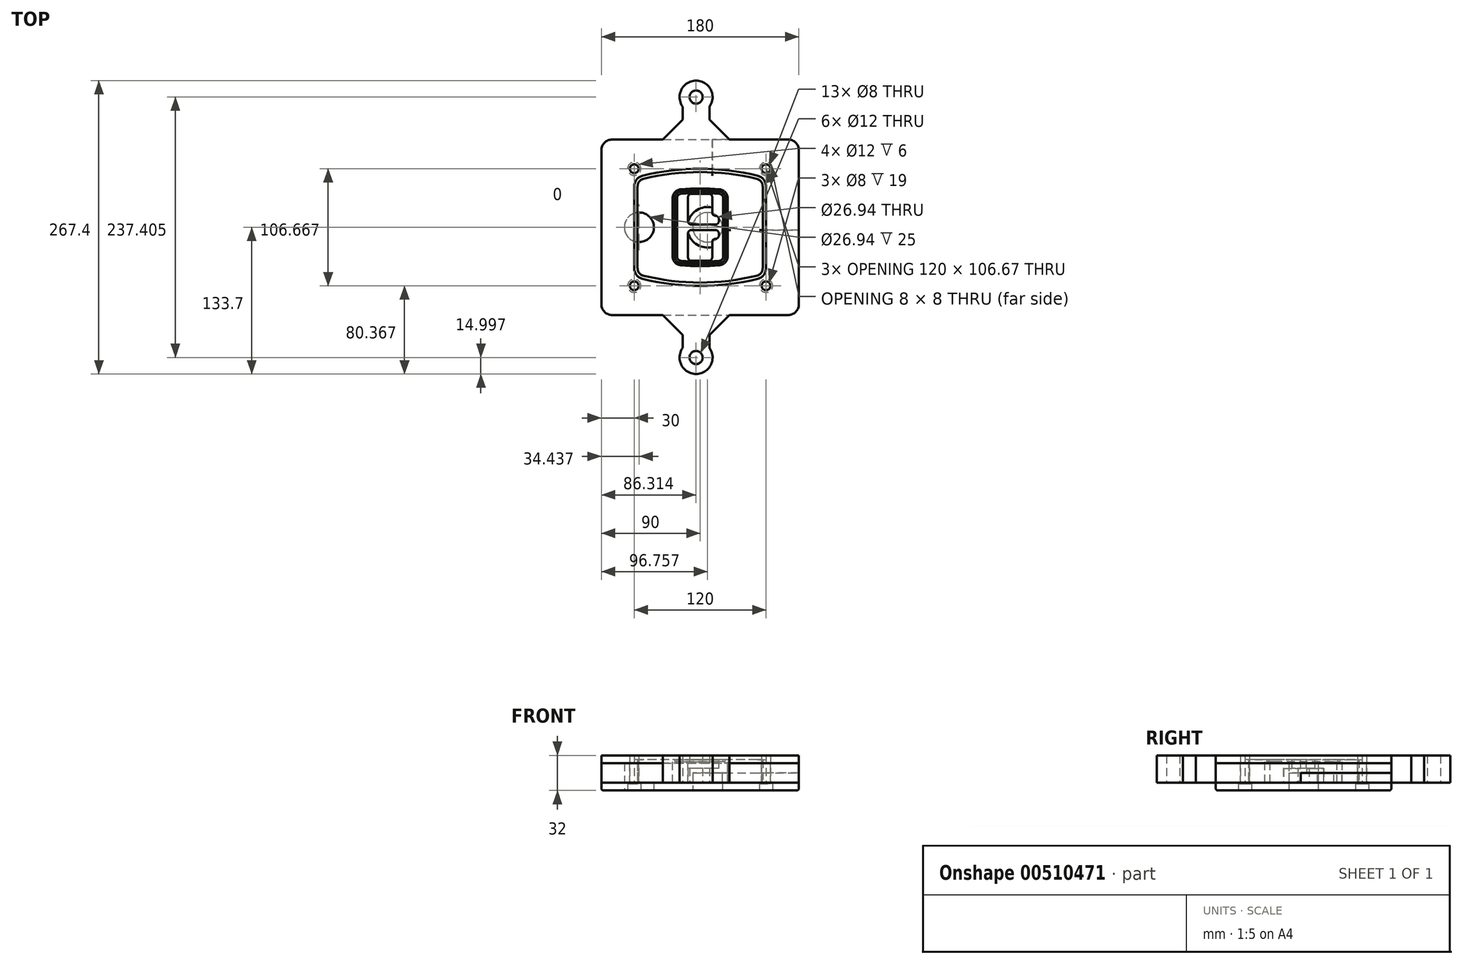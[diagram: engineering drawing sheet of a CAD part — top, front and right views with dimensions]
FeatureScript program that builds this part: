
annotation { "Feature Type Name" : "Feature", "Feature Type Description" : "" }
export const myFeature = defineFeature(function(context is Context, id is Id, definition is map)
    precondition{}
    {
        {
            var Q0;
            Q0=qCreatedBy(makeId("Top.planeOp"),FACE);
            var sketch = newSketch(context, id + "F0", { "sketchPlane" : qUnion([Q0])});
            skPoint(sketch, "E0.rect.middle", {"position": v(0, 0) * mm});
            skLineSegment(sketch, "E1.bottom", {"start": v(-80, -80) * mm, "end": v(80, -80) * mm});
            skLineSegment(sketch, "E1.top", {"start": v(-80, 80) * mm, "end": v(80, 80) * mm});
            skLineSegment(sketch, "E1.left", {"start": v(-90, -70) * mm, "end": v(-90, 70) * mm});
            skLineSegment(sketch, "E1.right", {"start": v(90, -70) * mm, "end": v(90, 70) * mm});
            skLineSegment(sketch, "E2", {"start": v(-90, 80) * mm, "end": v(90, -80) * mm, "construction": true});
            skLineSegment(sketch, "E3", {"start": v(90, 80) * mm, "end": v(-90, -80) * mm, "construction": true});
            skCircle(sketch, "E4", {"center": v(-60, 53.33) * mm, "radius": 4 * mm});
            skCircle(sketch, "E5", {"center": v(60, 53.33) * mm, "radius": 4 * mm});
            skCircle(sketch, "E6", {"center": v(60, -53.33) * mm, "radius": 4 * mm});
            skCircle(sketch, "E7", {"center": v(-60, -53.33) * mm, "radius": 4 * mm});
            skLineSegment(sketch, "E8", {"start": v(-60, 53.33) * mm, "end": v(60, 53.33) * mm, "construction": true});
            skLineSegment(sketch, "E9", {"start": v(60, 53.33) * mm, "end": v(60, -53.33) * mm, "construction": true});
            skLineSegment(sketch, "E10", {"start": v(60, -53.33) * mm, "end": v(-60, -53.33) * mm, "construction": true});
            skLineSegment(sketch, "E11", {"start": v(-60, -53.33) * mm, "end": v(-60, 53.33) * mm, "construction": true});
            skLineSegment(sketch, "E12", {"start": v(-60, 37.3) * mm, "end": v(-60, -37.3) * mm});
            skLineSegment(sketch, "E13", {"start": v(60, 37.3) * mm, "end": v(60, -37.3) * mm});
            skArc(sketch, "E14", {"start": v(52.38, 47.01) * mm, "mid": v(0, 53.33) * mm, "end": v(-52.38, 47.01) * mm});
            skArc(sketch, "E15", {"start": v(-52.38, -47.01) * mm, "mid": v(0, -53.33) * mm, "end": v(52.38, -47.01) * mm});
            skLineSegment(sketch, "E16", {"start": v(-60, 0) * mm, "end": v(60, 0) * mm, "construction": true});
            skPoint(sketch, "E17.visualSharp", {"position": v(-60, -45) * mm});
            skArc(sketch, "E17.filletArc", {"start": v(-60, -37.3) * mm, "mid": v(-57.87, -43.47) * mm, "end": v(-52.38, -47.01) * mm});
            skPoint(sketch, "E18.visualSharp", {"position": v(-60, 45) * mm});
            skArc(sketch, "E18.filletArc", {"start": v(-52.38, 47.01) * mm, "mid": v(-57.87, 43.47) * mm, "end": v(-60, 37.3) * mm});
            skPoint(sketch, "E19.visualSharp", {"position": v(60, 45) * mm});
            skArc(sketch, "E19.filletArc", {"start": v(60, 37.3) * mm, "mid": v(57.87, 43.47) * mm, "end": v(52.38, 47.01) * mm});
            skPoint(sketch, "E20.visualSharp", {"position": v(60, -45) * mm});
            skArc(sketch, "E20.filletArc", {"start": v(52.38, -47.01) * mm, "mid": v(57.87, -43.47) * mm, "end": v(60, -37.3) * mm});
            skPoint(sketch, "E21.visualSharp", {"position": v(-90, 80) * mm});
            skArc(sketch, "E21.filletArc", {"start": v(-80, 80) * mm, "mid": v(-87.07, 77.07) * mm, "end": v(-90, 70) * mm});
            skPoint(sketch, "E22.visualSharp", {"position": v(90, 80) * mm});
            skArc(sketch, "E22.filletArc", {"start": v(90, 70) * mm, "mid": v(87.07, 77.07) * mm, "end": v(80, 80) * mm});
            skPoint(sketch, "E23.visualSharp", {"position": v(90, -80) * mm});
            skArc(sketch, "E23.filletArc", {"start": v(80, -80) * mm, "mid": v(87.07, -77.07) * mm, "end": v(90, -70) * mm});
            skPoint(sketch, "E24.visualSharp", {"position": v(-90, -80) * mm});
            skArc(sketch, "E24.filletArc", {"start": v(-90, -70) * mm, "mid": v(-87.07, -77.07) * mm, "end": v(-80, -80) * mm});
            skArc(sketch, "E25.0", {"start": v(57, 37.3) * mm, "mid": v(55.5, 41.62) * mm, "end": v(51.67, 44.1) * mm});
            skLineSegment(sketch, "E25.1", {"start": v(57, 37.3) * mm, "end": v(57, -37.3) * mm});
            skArc(sketch, "E25.2", {"start": v(51.67, -44.1) * mm, "mid": v(55.5, -41.62) * mm, "end": v(57, -37.3) * mm});
            skArc(sketch, "E25.3", {"start": v(-51.67, -44.1) * mm, "mid": v(0, -50.33) * mm, "end": v(51.67, -44.1) * mm});
            skArc(sketch, "E25.4", {"start": v(-57, -37.3) * mm, "mid": v(-55.5, -41.62) * mm, "end": v(-51.67, -44.1) * mm});
            skArc(sketch, "E25.5", {"start": v(51.67, 44.1) * mm, "mid": v(0, 50.33) * mm, "end": v(-51.67, 44.1) * mm});
            skLineSegment(sketch, "E25.6", {"start": v(-57, 37.3) * mm, "end": v(-57, -37.3) * mm});
            skArc(sketch, "E25.7", {"start": v(-51.67, 44.1) * mm, "mid": v(-55.5, 41.62) * mm, "end": v(-57, 37.3) * mm});
            skArc(sketch, "E26.0", {"start": v(-53.33, 50.9) * mm, "mid": v(-61.01, 45.94) * mm, "end": v(-64, 37.3) * mm});
            skArc(sketch, "E26.1", {"start": v(53.33, 50.9) * mm, "mid": v(0, 57.33) * mm, "end": v(-53.33, 50.9) * mm});
            skArc(sketch, "E26.2", {"start": v(64, 37.3) * mm, "mid": v(61.01, 45.94) * mm, "end": v(53.33, 50.9) * mm});
            skLineSegment(sketch, "E26.3", {"start": v(64, 37.3) * mm, "end": v(64, -37.3) * mm});
            skArc(sketch, "E26.4", {"start": v(53.33, -50.9) * mm, "mid": v(61.01, -45.94) * mm, "end": v(64, -37.3) * mm});
            skLineSegment(sketch, "E26.5", {"start": v(-64, 37.3) * mm, "end": v(-64, -37.3) * mm});
            skArc(sketch, "E26.6", {"start": v(-53.33, -50.9) * mm, "mid": v(0, -57.33) * mm, "end": v(53.33, -50.9) * mm});
            skArc(sketch, "E26.7", {"start": v(-64, -37.3) * mm, "mid": v(-61.01, -45.94) * mm, "end": v(-53.33, -50.9) * mm});
            skSolve(sketch);
        }
        {
            var Q0;
            Q0=makeQuery(id+"F0.imprint","IMPRINT",FACE,{"disambiguationData":[TD([[makeQuery(id+"F0.imprint","IMPRINT",EDGE,{"derivedFrom":sQuery(id+"F0.wireOp",EDGE,"E1.bottom")}),1.0]])]});
            var Q1;
            Q1=makeQuery(id+"F0.imprint","IMPRINT",FACE,{"disambiguationData":[TD([[makeQuery(id+"F0.imprint","IMPRINT",EDGE,{"derivedFrom":sQuery(id+"F0.wireOp",EDGE,"E12")}),1.0]])]});
            var Q2;
            Q2=makeQuery(id+"F0.imprint","IMPRINT",FACE,{"disambiguationData":[TD([[makeQuery(id+"F0.imprint","IMPRINT",EDGE,{"derivedFrom":sQuery(id+"F0.wireOp",EDGE,"E25.0")}),1.0]])]});
            var Q3;
            Q3=makeQuery(id+"F0.imprint","IMPRINT",FACE,{"disambiguationData":[TD([[makeQuery(id+"F0.imprint","IMPRINT",EDGE,{"derivedFrom":sQuery(id+"F0.wireOp",EDGE,"E12")}),-1.0]])]});
            extrude(context, id + "F1", {"entities" : qUnion([Q0, Q1, Q2, Q3]), "oppositeDirection" : true, "depth" : 25 * mm});
        }
        {
            var Q0;
            Q0=makeQuery(id+"F0.imprint","IMPRINT",FACE,{"disambiguationData":[TD([[makeQuery(id+"F0.imprint","IMPRINT",EDGE,{"derivedFrom":sQuery(id+"F0.wireOp",EDGE,"E12")}),1.0]])]});
            extrude(context, id + "F2", {"entities" : qUnion([Q0]), "operationType" : NewBodyOperationType.ADD, "depth" : 3 * mm});
        }
        {
            var Q0;
            Q0=makeQuery(id+"F0.imprint","IMPRINT",FACE,{"disambiguationData":[TD([[makeQuery(id+"F0.imprint","IMPRINT",EDGE,{"derivedFrom":sQuery(id+"F0.wireOp",EDGE,"E25.0")}),1.0]])]});
            extrude(context, id + "F3", {"entities" : qUnion([Q0]), "operationType" : NewBodyOperationType.REMOVE, "oppositeDirection" : true, "depth" : 18 * mm});
        }
        {
            var Q0;
            Q0=makeQuery(id+"F2.opExtrude","CAP_FACE",FACE,{"disambiguationData":[OSD([sQuery(id+"F0.wireOp",EDGE,"E12"),sQuery(id+"F0.wireOp",EDGE,"E13"),sQuery(id+"F0.wireOp",EDGE,"E14"),sQuery(id+"F0.wireOp",EDGE,"E15"),sQuery(id+"F0.wireOp",EDGE,"E17.filletArc"),sQuery(id+"F0.wireOp",EDGE,"E18.filletArc"),sQuery(id+"F0.wireOp",EDGE,"E19.filletArc"),sQuery(id+"F0.wireOp",EDGE,"E20.filletArc"),sQuery(id+"F0.wireOp",EDGE,"E25.0"),sQuery(id+"F0.wireOp",EDGE,"E25.1"),sQuery(id+"F0.wireOp",EDGE,"E25.2"),sQuery(id+"F0.wireOp",EDGE,"E25.3"),sQuery(id+"F0.wireOp",EDGE,"E25.4"),sQuery(id+"F0.wireOp",EDGE,"E25.5"),sQuery(id+"F0.wireOp",EDGE,"E25.6"),sQuery(id+"F0.wireOp",EDGE,"E25.7")])],"isStart":false});
            var sketch = newSketch(context, id + "F4", { "sketchPlane" : qUnion([Q0])});
            skArc(sketch, "E27.0", {"start": v(-17.7, -34.56) * mm, "mid": v(0, -35.33) * mm, "end": v(17.7, -34.56) * mm});
            skArc(sketch, "E28.0", {"start": v(17.7, 34.56) * mm, "mid": v(0, 35.33) * mm, "end": v(-17.7, 34.56) * mm});
            skLineSegment(sketch, "E29", {"start": v(-25, 26.59) * mm, "end": v(-25, -26.59) * mm});
            skLineSegment(sketch, "E30", {"start": v(25, 26.59) * mm, "end": v(25, -26.59) * mm});
            skLineSegment(sketch, "E31", {"start": v(-25, 33.78) * mm, "end": v(25, 33.78) * mm, "construction": true});
            skLineSegment(sketch, "E32", {"start": v(-25, -33.78) * mm, "end": v(25, -33.78) * mm, "construction": true});
            skPoint(sketch, "E33.visualSharp", {"position": v(-25, 33.78) * mm});
            skArc(sketch, "E33.filletArc", {"start": v(-17.7, 34.56) * mm, "mid": v(-22.9, 32) * mm, "end": v(-25, 26.59) * mm});
            skPoint(sketch, "E34.visualSharp", {"position": v(25, 33.78) * mm});
            skArc(sketch, "E34.filletArc", {"start": v(25, 26.59) * mm, "mid": v(22.9, 32) * mm, "end": v(17.7, 34.56) * mm});
            skPoint(sketch, "E35.visualSharp", {"position": v(25, -33.78) * mm});
            skArc(sketch, "E35.filletArc", {"start": v(17.7, -34.56) * mm, "mid": v(22.9, -32) * mm, "end": v(25, -26.59) * mm});
            skPoint(sketch, "E36.visualSharp", {"position": v(-25, -33.78) * mm});
            skArc(sketch, "E36.filletArc", {"start": v(-25, -26.59) * mm, "mid": v(-22.9, -32) * mm, "end": v(-17.7, -34.56) * mm});
            skArc(sketch, "E37.0", {"start": v(51.67, 44.1) * mm, "mid": v(0, 50.33) * mm, "end": v(-51.67, 44.1) * mm});
            skArc(sketch, "E37.1", {"start": v(-51.67, 44.1) * mm, "mid": v(-55.5, 41.62) * mm, "end": v(-57, 37.3) * mm});
            skLineSegment(sketch, "E37.2", {"start": v(-57, 37.3) * mm, "end": v(-57, -37.3) * mm});
            skArc(sketch, "E37.3", {"start": v(-57, -37.3) * mm, "mid": v(-55.5, -41.62) * mm, "end": v(-51.67, -44.1) * mm});
            skArc(sketch, "E37.4", {"start": v(-51.67, -44.1) * mm, "mid": v(0, -50.33) * mm, "end": v(51.67, -44.1) * mm});
            skArc(sketch, "E37.5", {"start": v(51.67, -44.1) * mm, "mid": v(55.5, -41.62) * mm, "end": v(57, -37.3) * mm});
            skLineSegment(sketch, "E37.6", {"start": v(57, 37.3) * mm, "end": v(57, -37.3) * mm});
            skArc(sketch, "E37.7", {"start": v(57, 37.3) * mm, "mid": v(55.5, 41.62) * mm, "end": v(51.67, 44.1) * mm});
            skLineSegment(sketch, "E38.0", {"start": v(23, 26.59) * mm, "end": v(23, -26.59) * mm});
            skArc(sketch, "E38.1", {"start": v(17.53, -32.56) * mm, "mid": v(21.42, -30.64) * mm, "end": v(23, -26.59) * mm});
            skArc(sketch, "E38.2", {"start": v(-17.53, -32.56) * mm, "mid": v(0, -33.33) * mm, "end": v(17.53, -32.56) * mm});
            skArc(sketch, "E38.3", {"start": v(-23, -26.59) * mm, "mid": v(-21.42, -30.64) * mm, "end": v(-17.53, -32.56) * mm});
            skLineSegment(sketch, "E38.4", {"start": v(-23, 26.59) * mm, "end": v(-23, -26.59) * mm});
            skArc(sketch, "E38.5", {"start": v(23, 26.59) * mm, "mid": v(21.42, 30.64) * mm, "end": v(17.53, 32.56) * mm});
            skArc(sketch, "E38.6", {"start": v(-17.53, 32.56) * mm, "mid": v(-21.42, 30.64) * mm, "end": v(-23, 26.59) * mm});
            skArc(sketch, "E38.7", {"start": v(17.53, 32.56) * mm, "mid": v(0, 33.33) * mm, "end": v(-17.53, 32.56) * mm});
            skArc(sketch, "E39.0", {"start": v(21, 26.59) * mm, "mid": v(19.95, 29.29) * mm, "end": v(17.35, 30.57) * mm});
            skLineSegment(sketch, "E39.1", {"start": v(21, 26.59) * mm, "end": v(21, -26.59) * mm});
            skArc(sketch, "E39.2", {"start": v(17.35, -30.57) * mm, "mid": v(19.95, -29.29) * mm, "end": v(21, -26.59) * mm});
            skArc(sketch, "E39.3", {"start": v(-17.35, -30.57) * mm, "mid": v(0, -31.33) * mm, "end": v(17.35, -30.57) * mm});
            skArc(sketch, "E39.4", {"start": v(-21, -26.59) * mm, "mid": v(-19.95, -29.29) * mm, "end": v(-17.35, -30.57) * mm});
            skArc(sketch, "E39.5", {"start": v(17.35, 30.57) * mm, "mid": v(0, 31.33) * mm, "end": v(-17.35, 30.57) * mm});
            skLineSegment(sketch, "E39.6", {"start": v(-21, 26.59) * mm, "end": v(-21, -26.59) * mm});
            skArc(sketch, "E39.7", {"start": v(-17.35, 30.57) * mm, "mid": v(-19.95, 29.29) * mm, "end": v(-21, 26.59) * mm});
            skLineSegment(sketch, "E40", {"start": v(-25, 0) * mm, "end": v(25, 0) * mm, "construction": true});
            skLineSegment(sketch, "E41", {"start": v(-11, 5.5) * mm, "end": v(-11, 27.5) * mm});
            skLineSegment(sketch, "E42", {"start": v(-8, 30.5) * mm, "end": v(8, 30.5) * mm});
            skLineSegment(sketch, "E43", {"start": v(11, 27.5) * mm, "end": v(11, 13.5) * mm});
            skLineSegment(sketch, "E44", {"start": v(14, 10.5) * mm, "end": v(14, 10.5) * mm});
            skLineSegment(sketch, "E45", {"start": v(17, 7.5) * mm, "end": v(17, 5.5) * mm});
            skLineSegment(sketch, "E46", {"start": v(14, 2.5) * mm, "end": v(-8, 2.5) * mm});
            skPoint(sketch, "E47.visualSharp", {"position": v(-11, 30.5) * mm});
            skArc(sketch, "E47.filletArc", {"start": v(-8, 30.5) * mm, "mid": v(-10.12, 29.62) * mm, "end": v(-11, 27.5) * mm});
            skPoint(sketch, "E48.visualSharp", {"position": v(11, 30.5) * mm});
            skArc(sketch, "E48.filletArc", {"start": v(11, 27.5) * mm, "mid": v(10.12, 29.62) * mm, "end": v(8, 30.5) * mm});
            skPoint(sketch, "E49.visualSharp", {"position": v(11, 10.5) * mm});
            skArc(sketch, "E49.filletArc", {"start": v(11, 13.5) * mm, "mid": v(11.88, 11.38) * mm, "end": v(14, 10.5) * mm});
            skPoint(sketch, "E50.visualSharp", {"position": v(17, 10.5) * mm});
            skArc(sketch, "E50.filletArc", {"start": v(17, 7.5) * mm, "mid": v(16.12, 9.62) * mm, "end": v(14, 10.5) * mm});
            skPoint(sketch, "E51.visualSharp", {"position": v(17, 2.5) * mm});
            skArc(sketch, "E51.filletArc", {"start": v(14, 2.5) * mm, "mid": v(16.12, 3.38) * mm, "end": v(17, 5.5) * mm});
            skPoint(sketch, "E52.visualSharp", {"position": v(-11, 2.5) * mm});
            skArc(sketch, "E52.filletArc", {"start": v(-11, 5.5) * mm, "mid": v(-10.12, 3.38) * mm, "end": v(-8, 2.5) * mm});
            skLineSegment(sketch, "E53.0.MirrorCS", {"start": v(14, -2.5) * mm, "end": v(-8, -2.5) * mm});
            skArc(sketch, "E54.0.MirrorCS", {"start": v(-11, -5.5) * mm, "mid": v(-10.12, -3.38) * mm, "end": v(-8, -2.5) * mm});
            skLineSegment(sketch, "E55.0.MirrorCS", {"start": v(-11, -5.5) * mm, "end": v(-11, -27.5) * mm});
            skArc(sketch, "E56.0.MirrorCS", {"start": v(-8, -30.5) * mm, "mid": v(-10.12, -29.62) * mm, "end": v(-11, -27.5) * mm});
            skLineSegment(sketch, "E57.0.MirrorCS", {"start": v(-8, -30.5) * mm, "end": v(8, -30.5) * mm});
            skArc(sketch, "E58.0.MirrorCS", {"start": v(11, -27.5) * mm, "mid": v(10.12, -29.62) * mm, "end": v(8, -30.5) * mm});
            skLineSegment(sketch, "E59.0.MirrorCS", {"start": v(11, -27.5) * mm, "end": v(11, -13.5) * mm});
            skArc(sketch, "E60.0.MirrorCS", {"start": v(11, -13.5) * mm, "mid": v(11.88, -11.38) * mm, "end": v(14, -10.5) * mm});
            skArc(sketch, "E61.0.MirrorCS", {"start": v(17, -7.5) * mm, "mid": v(16.12, -9.62) * mm, "end": v(14, -10.5) * mm});
            skLineSegment(sketch, "E62.0.MirrorCS", {"start": v(17, -7.5) * mm, "end": v(17, -5.5) * mm});
            skArc(sketch, "E63.0.MirrorCS", {"start": v(14, -2.5) * mm, "mid": v(16.12, -3.38) * mm, "end": v(17, -5.5) * mm});
            skSolve(sketch);
        }
        {
            var Q0;
            Q0=makeQuery(id+"F4.imprint","IMPRINT",FACE,{"disambiguationData":[TD([[makeQuery(id+"F4.imprint","IMPRINT",EDGE,{"derivedFrom":sQuery(id+"F4.wireOp",EDGE,"E27.0")}),1.0]])]});
            var Q1;
            Q1=makeQuery(id+"F4.imprint","IMPRINT",FACE,{"disambiguationData":[TD([[makeQuery(id+"F4.imprint","IMPRINT",EDGE,{"derivedFrom":sQuery(id+"F4.wireOp",EDGE,"E38.0")}),-1.0]])]});
            var Q2;
            Q2=makeQuery(id+"F4.imprint","IMPRINT",FACE,{"disambiguationData":[TD([[makeQuery(id+"F4.imprint","IMPRINT",EDGE,{"derivedFrom":sQuery(id+"F4.wireOp",EDGE,"E39.0")}),1.0]])]});
            extrude(context, id + "F5", {"entities" : qUnion([Q0, Q1, Q2]), "operationType" : NewBodyOperationType.ADD, "endBound" : BoundingType.UP_TO_NEXT, "oppositeDirection" : true, "depth" : 25 * mm});
        }
        {
            var Q0;
            Q0=makeQuery(id+"F4.imprint","IMPRINT",FACE,{"disambiguationData":[TD([[makeQuery(id+"F4.imprint","IMPRINT",EDGE,{"derivedFrom":sQuery(id+"F4.wireOp",EDGE,"E38.0")}),-1.0]])]});
            extrude(context, id + "F6", {"entities" : qUnion([Q0]), "operationType" : NewBodyOperationType.REMOVE, "oppositeDirection" : true, "depth" : 2 * mm});
        }
        {
            var Q0;
            Q0=makeQuery(id+"F1.opExtrude","CAP_FACE",FACE,{"disambiguationData":[OSD([sQuery(id+"F0.wireOp",EDGE,"E1.bottom"),sQuery(id+"F0.wireOp",EDGE,"E1.top"),sQuery(id+"F0.wireOp",EDGE,"E1.left"),sQuery(id+"F0.wireOp",EDGE,"E1.right"),sQuery(id+"F0.wireOp",EDGE,"E4"),sQuery(id+"F0.wireOp",EDGE,"E5"),sQuery(id+"F0.wireOp",EDGE,"E6"),sQuery(id+"F0.wireOp",EDGE,"E7"),sQuery(id+"F0.wireOp",EDGE,"E21.filletArc"),sQuery(id+"F0.wireOp",EDGE,"E22.filletArc"),sQuery(id+"F0.wireOp",EDGE,"E23.filletArc"),sQuery(id+"F0.wireOp",EDGE,"E24.filletArc")])],"isStart":false});
            var sketch = newSketch(context, id + "F7", { "sketchPlane" : qUnion([Q0])});
            skCircle(sketch, "E64", {"center": v(6.76, 0) * mm, "radius": 13.47 * mm});
            skCircle(sketch, "E65", {"center": v(-55.56, 0) * mm, "radius": 13.47 * mm});
            skLineSegment(sketch, "E66", {"start": v(90, 0) * mm, "end": v(-90, 0) * mm});
            skCircle(sketch, "E67", {"center": v(6.76, 0) * mm, "radius": 18.47 * mm});
            skCircle(sketch, "E68", {"center": v(60, -53.33) * mm, "radius": 6 * mm});
            skCircle(sketch, "E69", {"center": v(-60, -53.33) * mm, "radius": 6 * mm});
            skCircle(sketch, "E70", {"center": v(-60, 53.33) * mm, "radius": 6 * mm});
            skCircle(sketch, "E71", {"center": v(60, 53.33) * mm, "radius": 6 * mm});
            skSolve(sketch);
        }
        {
            var Q0;
            {var subQ1=sQuery(id+"F7.wireOp",EDGE,"E66");var subQ4=sQuery(id+"F7.wireOp",EDGE,"E64");var subQ6=makeQuery(id+"F7.imprint","INTERSECT",VERTEX,{"disambiguationData":[OD(0.0)],"derivedFrom":[subQ4,subQ1]});Q0=makeQuery(id+"F7.imprint","IMPRINT",FACE,{"disambiguationData":[TD([[makeQuery(id+"F7.imprint","IMPRINT",EDGE,{"disambiguationData":[TD([[subQ6,-1.0]])],"derivedFrom":subQ4}),-1.0]])]});}
            var Q1;
            {var subQ0=sQuery(id+"F7.wireOp",EDGE,"E66");var subQ1=sQuery(id+"F7.wireOp",EDGE,"E64");var subQ3=makeQuery(id+"F7.imprint","INTERSECT",VERTEX,{"disambiguationData":[OD(0.0)],"derivedFrom":[subQ1,subQ0]});Q1=makeQuery(id+"F7.imprint","IMPRINT",FACE,{"disambiguationData":[TD([[makeQuery(id+"F7.imprint","IMPRINT",EDGE,{"disambiguationData":[TD([[subQ3,-1.0]])],"derivedFrom":subQ1}),1.0]])]});}
            var Q2;
            {var subQ0=sQuery(id+"F7.wireOp",EDGE,"E66");var subQ1=sQuery(id+"F7.wireOp",EDGE,"E64");var subQ3=makeQuery(id+"F7.imprint","INTERSECT",VERTEX,{"disambiguationData":[OD(0.0)],"derivedFrom":[subQ1,subQ0]});Q2=makeQuery(id+"F7.imprint","IMPRINT",FACE,{"disambiguationData":[TD([[makeQuery(id+"F7.imprint","IMPRINT",EDGE,{"disambiguationData":[TD([[subQ3,1.0]])],"derivedFrom":subQ1}),1.0]])]});}
            var Q3;
            {var subQ1=sQuery(id+"F7.wireOp",EDGE,"E66");var subQ4=sQuery(id+"F7.wireOp",EDGE,"E64");var subQ6=makeQuery(id+"F7.imprint","INTERSECT",VERTEX,{"disambiguationData":[OD(0.0)],"derivedFrom":[subQ4,subQ1]});Q3=makeQuery(id+"F7.imprint","IMPRINT",FACE,{"disambiguationData":[TD([[makeQuery(id+"F7.imprint","IMPRINT",EDGE,{"disambiguationData":[TD([[subQ6,1.0]])],"derivedFrom":subQ4}),-1.0]])]});}
            extrude(context, id + "F8", {"entities" : qUnion([Q0, Q1, Q2, Q3]), "operationType" : NewBodyOperationType.ADD, "oppositeDirection" : true, "depth" : 20 * mm});
        }
        {
            var Q0;
            {var subQ0=sQuery(id+"F7.wireOp",EDGE,"E66");var subQ1=sQuery(id+"F7.wireOp",EDGE,"E64");var subQ3=makeQuery(id+"F7.imprint","INTERSECT",VERTEX,{"disambiguationData":[OD(0.0)],"derivedFrom":[subQ1,subQ0]});Q0=makeQuery(id+"F7.imprint","IMPRINT",FACE,{"disambiguationData":[TD([[makeQuery(id+"F7.imprint","IMPRINT",EDGE,{"disambiguationData":[TD([[subQ3,-1.0]])],"derivedFrom":subQ1}),1.0]])]});}
            var Q1;
            {var subQ0=sQuery(id+"F7.wireOp",EDGE,"E66");var subQ1=sQuery(id+"F7.wireOp",EDGE,"E64");var subQ3=makeQuery(id+"F7.imprint","INTERSECT",VERTEX,{"disambiguationData":[OD(0.0)],"derivedFrom":[subQ1,subQ0]});Q1=makeQuery(id+"F7.imprint","IMPRINT",FACE,{"disambiguationData":[TD([[makeQuery(id+"F7.imprint","IMPRINT",EDGE,{"disambiguationData":[TD([[subQ3,1.0]])],"derivedFrom":subQ1}),1.0]])]});}
            extrude(context, id + "F9", {"entities" : qUnion([Q0, Q1]), "operationType" : NewBodyOperationType.REMOVE, "oppositeDirection" : true, "depth" : 16 * mm});
        }
        {
            var Q0;
            {var subQ0=sQuery(id+"F7.wireOp",EDGE,"E66");var subQ1=sQuery(id+"F7.wireOp",EDGE,"E65");var subQ3=makeQuery(id+"F7.imprint","INTERSECT",VERTEX,{"disambiguationData":[OD(0.0)],"derivedFrom":[subQ1,subQ0]});Q0=makeQuery(id+"F7.imprint","IMPRINT",FACE,{"disambiguationData":[TD([[makeQuery(id+"F7.imprint","IMPRINT",EDGE,{"disambiguationData":[TD([[subQ3,-1.0]])],"derivedFrom":subQ1}),1.0]])]});}
            var Q1;
            {var subQ0=sQuery(id+"F7.wireOp",EDGE,"E66");var subQ1=sQuery(id+"F7.wireOp",EDGE,"E65");var subQ3=makeQuery(id+"F7.imprint","INTERSECT",VERTEX,{"disambiguationData":[OD(0.0)],"derivedFrom":[subQ1,subQ0]});Q1=makeQuery(id+"F7.imprint","IMPRINT",FACE,{"disambiguationData":[TD([[makeQuery(id+"F7.imprint","IMPRINT",EDGE,{"disambiguationData":[TD([[subQ3,1.0]])],"derivedFrom":subQ1}),1.0]])]});}
            extrude(context, id + "F10", {"entities" : qUnion([Q0, Q1]), "operationType" : NewBodyOperationType.REMOVE, "oppositeDirection" : true, "depth" : 25 * mm});
        }
        {
            var Q0;
            Q0=makeQuery(id+"F7.imprint","IMPRINT",FACE,{"disambiguationData":[TD([[makeQuery(id+"F7.imprint","IMPRINT",EDGE,{"derivedFrom":sQuery(id+"F7.wireOp",EDGE,"E68")}),1.0]])]});
            var Q1;
            Q1=makeQuery(id+"F7.imprint","IMPRINT",FACE,{"disambiguationData":[TD([[makeQuery(id+"F7.imprint","IMPRINT",EDGE,{"derivedFrom":makeQuery(id+"F1.opExtrude","CAP_EDGE",EDGE,{"disambiguationData":[OSD([sQuery(id+"F0.wireOp",EDGE,"E5")])],"isStart":false})}),-1.0]])]});
            var Q2;
            Q2=makeQuery(id+"F7.imprint","IMPRINT",FACE,{"disambiguationData":[TD([[makeQuery(id+"F7.imprint","IMPRINT",EDGE,{"derivedFrom":sQuery(id+"F7.wireOp",EDGE,"E69")}),1.0]])]});
            var Q3;
            Q3=makeQuery(id+"F7.imprint","IMPRINT",FACE,{"disambiguationData":[TD([[makeQuery(id+"F7.imprint","IMPRINT",EDGE,{"derivedFrom":makeQuery(id+"F1.opExtrude","CAP_EDGE",EDGE,{"disambiguationData":[OSD([sQuery(id+"F0.wireOp",EDGE,"E4")])],"isStart":false})}),-1.0]])]});
            var Q4;
            Q4=makeQuery(id+"F7.imprint","IMPRINT",FACE,{"disambiguationData":[TD([[makeQuery(id+"F7.imprint","IMPRINT",EDGE,{"derivedFrom":sQuery(id+"F7.wireOp",EDGE,"E70")}),1.0]])]});
            var Q5;
            Q5=makeQuery(id+"F7.imprint","IMPRINT",FACE,{"disambiguationData":[TD([[makeQuery(id+"F7.imprint","IMPRINT",EDGE,{"derivedFrom":makeQuery(id+"F1.opExtrude","CAP_EDGE",EDGE,{"disambiguationData":[OSD([sQuery(id+"F0.wireOp",EDGE,"E7")])],"isStart":false})}),-1.0]])]});
            var Q6;
            Q6=makeQuery(id+"F7.imprint","IMPRINT",FACE,{"disambiguationData":[TD([[makeQuery(id+"F7.imprint","IMPRINT",EDGE,{"derivedFrom":sQuery(id+"F7.wireOp",EDGE,"E71")}),1.0]])]});
            var Q7;
            Q7=makeQuery(id+"F7.imprint","IMPRINT",FACE,{"disambiguationData":[TD([[makeQuery(id+"F7.imprint","IMPRINT",EDGE,{"derivedFrom":makeQuery(id+"F1.opExtrude","CAP_EDGE",EDGE,{"disambiguationData":[OSD([sQuery(id+"F0.wireOp",EDGE,"E6")])],"isStart":false})}),-1.0]])]});
            extrude(context, id + "F11", {"entities" : qUnion([Q0, Q1, Q2, Q3, Q4, Q5, Q6, Q7]), "operationType" : NewBodyOperationType.REMOVE, "oppositeDirection" : true, "depth" : 6 * mm});
        }
        {
            var Q0;
            Q0=makeQuery(id+"F9.boolean.opBoolean","COPY",FACE,{"derivedFrom":makeQuery(id+"F9.opExtrude","CAP_FACE",FACE,{"disambiguationData":[OSD([sQuery(id+"F7.wireOp",EDGE,"E64")])],"isStart":false})});
            var sketch = newSketch(context, id + "F12", { "sketchPlane" : qUnion([Q0])});
            skArc(sketch, "E72.0", {"start": v(11, -88.19) * mm, "mid": v(97.1, -83.6) * mm, "end": v(92.5, 2.5) * mm});
            skLineSegment(sketch, "E72.1", {"start": v(11, -17.97) * mm, "end": v(11, -17.97) * mm});
            skLineSegment(sketch, "E73", {"start": v(92.5, -105.13) * mm, "end": v(102.3, -105.13) * mm});
            skLineSegment(sketch, "E74.0", {"start": v(92.5, 2.5) * mm, "end": v(14, 2.5) * mm});
            skArc(sketch, "E74.1", {"start": v(14, 2.5) * mm, "mid": v(16.12, 3.38) * mm, "end": v(17, 5.5) * mm});
            skLineSegment(sketch, "E74.2", {"start": v(17, 7.5) * mm, "end": v(17, 5.5) * mm});
            skArc(sketch, "E74.3", {"start": v(17, 7.5) * mm, "mid": v(16.12, 9.62) * mm, "end": v(14, 10.5) * mm});
            skArc(sketch, "E74.4", {"start": v(11, 13.5) * mm, "mid": v(11.88, 11.38) * mm, "end": v(14, 10.5) * mm});
            skLineSegment(sketch, "E74.5", {"start": v(11, 13.5) * mm, "end": v(11, -88.19) * mm});
            skLineSegment(sketch, "E74.7", {"start": v(92.5, -2.5) * mm, "end": v(14, -2.5) * mm});
            skArc(sketch, "E74.8", {"start": v(14, -2.5) * mm, "mid": v(16.12, -3.38) * mm, "end": v(17, -5.5) * mm});
            skLineSegment(sketch, "E74.9", {"start": v(17, -7.5) * mm, "end": v(17, -5.5) * mm});
            skArc(sketch, "E74.10", {"start": v(17, -7.5) * mm, "mid": v(16.12, -9.62) * mm, "end": v(14, -10.5) * mm});
            skArc(sketch, "E74.11", {"start": v(11, -13.5) * mm, "mid": v(11.88, -11.38) * mm, "end": v(14, -10.5) * mm});
            skLineSegment(sketch, "E74.12", {"start": v(11, -17.97) * mm, "end": v(11, -13.5) * mm});
            skPoint(sketch, "E75.orphan", {"position": v(11, -27.5) * mm});
            skPoint(sketch, "E76.orphan", {"position": v(-8, -2.5) * mm});
            skPoint(sketch, "E77.orphan", {"position": v(-8, 2.5) * mm});
            skPoint(sketch, "E78.orphan", {"position": v(11, 27.5) * mm});
            skSolve(sketch);
        }
        {
            var Q0;
            {var subQ7=sQuery(id+"F12.wireOp",EDGE,"E72.0");var subQ14=sQuery(id+"F12.wireOp",EDGE,"E72.1");var subQ16=sQuery(id+"F12.wireOp",EDGE,"E74.1");var subQ18=sQuery(id+"F12.wireOp",EDGE,"E74.8");Q0=qUnion([makeQuery(id+"F12.imprint","IMPRINT",FACE,{"disambiguationData":[TD([[makeQuery(id+"F12.imprint","IMPRINT",EDGE,{"derivedFrom":subQ7}),1.0]])]}),makeQuery(id+"F12.imprint","IMPRINT",FACE,{"disambiguationData":[TD([[makeQuery(id+"F12.imprint","IMPRINT",EDGE,{"derivedFrom":subQ14}),1.0]])]}),makeQuery(id+"F12.imprint","IMPRINT",FACE,{"disambiguationData":[TD([[makeQuery(id+"F12.imprint","IMPRINT",EDGE,{"derivedFrom":subQ16}),1.0]])]}),makeQuery(id+"F12.imprint","IMPRINT",FACE,{"disambiguationData":[TD([[makeQuery(id+"F12.imprint","IMPRINT",EDGE,{"derivedFrom":subQ18}),-1.0]])]})]);}
            var Q1;
            Q1=makeQuery(id+"F5.boolean.opBoolean","SPLIT",FACE,{"disambiguationData":[TD([makeQuery(id+"F5.opExtrude","SWEPT_FACE",FACE,{"disambiguationData":[OSD([sQuery(id+"F4.wireOp",EDGE,"E41")])]})])],"derivedFrom":makeQuery(id+"F3.boolean.opBoolean","COPY",FACE,{"derivedFrom":makeQuery(id+"F3.opExtrude","CAP_FACE",FACE,{"disambiguationData":[OSD([sQuery(id+"F0.wireOp",EDGE,"E25.0"),sQuery(id+"F0.wireOp",EDGE,"E25.1"),sQuery(id+"F0.wireOp",EDGE,"E25.2"),sQuery(id+"F0.wireOp",EDGE,"E25.3"),sQuery(id+"F0.wireOp",EDGE,"E25.4"),sQuery(id+"F0.wireOp",EDGE,"E25.5"),sQuery(id+"F0.wireOp",EDGE,"E25.6"),sQuery(id+"F0.wireOp",EDGE,"E25.7")])],"isStart":false})})});
            extrude(context, id + "F13", {"entities" : qUnion([Q0]), "operationType" : NewBodyOperationType.REMOVE, "endBound" : BoundingType.UP_TO_SURFACE, "endBoundEntityFace" : qUnion([Q1]), "depth" : 25 * mm});
        }
        {
            var Q0;
            Q0=makeQuery(id+"F3.boolean.opBoolean","COPY",EDGE,{"derivedFrom":makeQuery(id+"F3.opExtrude","CAP_EDGE",EDGE,{"disambiguationData":[OSD([sQuery(id+"F0.wireOp",EDGE,"E25.6")])],"isStart":false})});
            var Q1;
            Q1=makeQuery(id+"F8.boolean.opBoolean","INTERSECT",EDGE,{"derivedFrom":[makeQuery(id+"F5.opExtrude","SWEPT_FACE",FACE,{"disambiguationData":[OSD([sQuery(id+"F4.wireOp",EDGE,"E30")])]}),makeQuery(id+"F8.opExtrude","CAP_FACE",FACE,{"disambiguationData":[OSD([sQuery(id+"F7.wireOp",EDGE,"E67")])],"isStart":false})]});
            var Q2;
            Q2=makeQuery(id+"F8.boolean.opBoolean","INTERSECT",EDGE,{"disambiguationData":[OD(1.0)],"derivedFrom":[makeQuery(id+"F5.opExtrude","SWEPT_FACE",FACE,{"disambiguationData":[OSD([sQuery(id+"F4.wireOp",EDGE,"E30")])]}),makeQuery(id+"F8.opExtrude","SWEPT_FACE",FACE,{"disambiguationData":[OSD([sQuery(id+"F7.wireOp",EDGE,"E67")])]})]});
            var Q3;
            {var subQ0=makeQuery(id+"F3.boolean.opBoolean","COPY",FACE,{"derivedFrom":makeQuery(id+"F3.opExtrude","CAP_FACE",FACE,{"disambiguationData":[OSD([sQuery(id+"F0.wireOp",EDGE,"E25.0"),sQuery(id+"F0.wireOp",EDGE,"E25.1"),sQuery(id+"F0.wireOp",EDGE,"E25.2"),sQuery(id+"F0.wireOp",EDGE,"E25.3"),sQuery(id+"F0.wireOp",EDGE,"E25.4"),sQuery(id+"F0.wireOp",EDGE,"E25.5"),sQuery(id+"F0.wireOp",EDGE,"E25.6"),sQuery(id+"F0.wireOp",EDGE,"E25.7")])],"isStart":false})});var subQ1=sQuery(id+"F4.wireOp",EDGE,"E30");Q3=makeQuery(id+"F8.boolean.opBoolean","SPLIT",EDGE,{"disambiguationData":[TD([makeQuery(id+"F5.opExtrude","SWEPT_FACE",FACE,{"disambiguationData":[OSD([sQuery(id+"F4.wireOp",EDGE,"E35.filletArc")])]})])],"derivedFrom":makeQuery(id+"F5.opExtrude","TWEAK_EDGE",EDGE,{"derivedFrom":[subQ0,makeQuery(id+"F4.imprint","IMPRINT",EDGE,{"derivedFrom":subQ1})]})});}
            var Q4;
            {var subQ0=sQuery(id+"F0.wireOp",EDGE,"E25.0");var subQ1=sQuery(id+"F0.wireOp",EDGE,"E25.1");var subQ2=sQuery(id+"F0.wireOp",EDGE,"E25.2");var subQ3=sQuery(id+"F0.wireOp",EDGE,"E25.3");var subQ4=sQuery(id+"F0.wireOp",EDGE,"E25.4");var subQ5=sQuery(id+"F0.wireOp",EDGE,"E25.5");var subQ6=sQuery(id+"F0.wireOp",EDGE,"E25.6");var subQ7=sQuery(id+"F0.wireOp",EDGE,"E25.7");Q4=makeQuery(id+"F8.boolean.opBoolean","INTERSECT",EDGE,{"derivedFrom":[makeQuery(id+"F5.boolean.opBoolean","SPLIT",FACE,{"disambiguationData":[TD([makeQuery(id+"F2.opExtrude","SWEPT_FACE",FACE,{"disambiguationData":[OSD([subQ0])]})])],"derivedFrom":makeQuery(id+"F3.boolean.opBoolean","COPY",FACE,{"derivedFrom":makeQuery(id+"F3.opExtrude","CAP_FACE",FACE,{"disambiguationData":[OSD([subQ0,subQ1,subQ2,subQ3,subQ4,subQ5,subQ6,subQ7])],"isStart":false})})}),makeQuery(id+"F8.opExtrude","SWEPT_FACE",FACE,{"disambiguationData":[OSD([sQuery(id+"F7.wireOp",EDGE,"E67")])]})]});}
            var Q5;
            Q5=makeQuery(id+"F8.boolean.opBoolean","INTERSECT",EDGE,{"disambiguationData":[OD(0.0)],"derivedFrom":[makeQuery(id+"F5.opExtrude","SWEPT_FACE",FACE,{"disambiguationData":[OSD([sQuery(id+"F4.wireOp",EDGE,"E30")])]}),makeQuery(id+"F8.opExtrude","SWEPT_FACE",FACE,{"disambiguationData":[OSD([sQuery(id+"F7.wireOp",EDGE,"E67")])]})]});
            fillet(context, id + "F14", {"entities" : qUnion([Q0, Q1, Q2, Q3, Q4, Q5]), "radius" : 3 * mm, "tangentPropagation" : true, "allowEdgeOverflow" : false});
        }
        {
            var Q0;
            Q0=makeQuery(id+"F1.opExtrude","CAP_EDGE",EDGE,{"disambiguationData":[OSD([sQuery(id+"F0.wireOp",EDGE,"E1.bottom")])],"isStart":false});
            fillet(context, id + "F15", {"entities" : qUnion([Q0]), "radius" : 2 * mm, "tangentPropagation" : true, "allowEdgeOverflow" : false});
        }
        {
            var Q0;
            {var subQ0=sQuery(id+"F0.wireOp",EDGE,"E25.5");var subQ1=sQuery(id+"F0.wireOp",EDGE,"E25.0");var subQ2=sQuery(id+"F0.wireOp",EDGE,"E25.7");var subQ3=sQuery(id+"F0.wireOp",EDGE,"E25.2");var subQ4=sQuery(id+"F0.wireOp",EDGE,"E25.6");var subQ5=sQuery(id+"F0.wireOp",EDGE,"E25.1");var subQ6=sQuery(id+"F0.wireOp",EDGE,"E25.4");var subQ7=sQuery(id+"F0.wireOp",EDGE,"E25.3");Q0=makeQuery(id+"F5.boolean.opBoolean","SPLIT",FACE,{"disambiguationData":[TD([makeQuery(id+"F2.opExtrude","SWEPT_FACE",FACE,{"disambiguationData":[OSD([subQ1])]})])],"derivedFrom":makeQuery(id+"F3.boolean.opBoolean","COPY",FACE,{"derivedFrom":makeQuery(id+"F3.opExtrude","CAP_FACE",FACE,{"disambiguationData":[OSD([subQ1,subQ5,subQ3,subQ7,subQ6,subQ0,subQ4,subQ2])],"isStart":false})})});}
            var sketch = newSketch(context, id + "F16", { "sketchPlane" : qUnion([Q0])});
            skLineSegment(sketch, "E79.0", {"start": v(-80, 80) * mm, "end": v(80, 80) * mm});
            skArc(sketch, "E79.1", {"start": v(90, 70) * mm, "mid": v(87.07, 77.07) * mm, "end": v(80, 80) * mm});
            skLineSegment(sketch, "E79.2", {"start": v(90, -70) * mm, "end": v(90, 70) * mm});
            skArc(sketch, "E79.3", {"start": v(80, -80) * mm, "mid": v(87.07, -77.07) * mm, "end": v(90, -70) * mm});
            skLineSegment(sketch, "E79.4", {"start": v(-80, -80) * mm, "end": v(80, -80) * mm});
            skArc(sketch, "E79.5", {"start": v(-90, -70) * mm, "mid": v(-87.07, -77.07) * mm, "end": v(-80, -80) * mm});
            skLineSegment(sketch, "E79.6", {"start": v(-90, -70) * mm, "end": v(-90, 70) * mm});
            skCircle(sketch, "E79.7", {"center": v(-60, -53.33) * mm, "radius": 4 * mm});
            skCircle(sketch, "E79.8", {"center": v(-60, 53.33) * mm, "radius": 4 * mm});
            skArc(sketch, "E79.9", {"start": v(-80, 80) * mm, "mid": v(-87.07, 77.07) * mm, "end": v(-90, 70) * mm});
            skCircle(sketch, "E79.10", {"center": v(60, -53.33) * mm, "radius": 4 * mm});
            skCircle(sketch, "E79.11", {"center": v(60, 53.33) * mm, "radius": 4 * mm});
            skArc(sketch, "E79.12", {"start": v(52.38, 47.01) * mm, "mid": v(0, 53.33) * mm, "end": v(-52.38, 47.01) * mm});
            skArc(sketch, "E79.13", {"start": v(60, 37.3) * mm, "mid": v(57.87, 43.47) * mm, "end": v(52.38, 47.01) * mm});
            skLineSegment(sketch, "E79.14", {"start": v(60, 37.3) * mm, "end": v(60, -37.3) * mm});
            skArc(sketch, "E79.15", {"start": v(52.38, -47.01) * mm, "mid": v(57.87, -43.47) * mm, "end": v(60, -37.3) * mm});
            skArc(sketch, "E79.16", {"start": v(-52.38, -47.01) * mm, "mid": v(0, -53.33) * mm, "end": v(52.38, -47.01) * mm});
            skArc(sketch, "E79.17", {"start": v(-60, -37.3) * mm, "mid": v(-57.87, -43.47) * mm, "end": v(-52.38, -47.01) * mm});
            skLineSegment(sketch, "E79.18", {"start": v(-60, 37.3) * mm, "end": v(-60, -37.3) * mm});
            skArc(sketch, "E79.19", {"start": v(-52.38, 47.01) * mm, "mid": v(-57.87, 43.47) * mm, "end": v(-60, 37.3) * mm});
            skLineSegment(sketch, "E80", {"start": v(-33.9, 80) * mm, "end": v(-15.9, 98) * mm});
            skLineSegment(sketch, "E81", {"start": v(-15.9, 98) * mm, "end": v(-15.9, 110) * mm});
            skLineSegment(sketch, "E82", {"start": v(8.53, 98) * mm, "end": v(26.53, 80) * mm});
            skLineSegment(sketch, "E83", {"start": v(8.53, 98) * mm, "end": v(8.53, 110) * mm});
            skArc(sketch, "E84", {"start": v(8.53, 110) * mm, "mid": v(-3.69, 133.7) * mm, "end": v(-15.9, 110) * mm});
            skCircle(sketch, "E85", {"center": v(-3.69, 118.7) * mm, "radius": 6 * mm});
            skLineSegment(sketch, "E86", {"start": v(-3.69, 118.7) * mm, "end": v(-3.69, 80) * mm, "construction": true});
            skLineSegment(sketch, "E87", {"start": v(-90, 0) * mm, "end": v(90, 0) * mm, "construction": true});
            skLineSegment(sketch, "E88.MirrorCS", {"start": v(8.53, -98) * mm, "end": v(26.53, -80) * mm});
            skLineSegment(sketch, "E89.MirrorCS", {"start": v(8.53, -98) * mm, "end": v(8.53, -110) * mm});
            skArc(sketch, "E90.MirrorCS", {"start": v(8.53, -110) * mm, "mid": v(-3.69, -133.7) * mm, "end": v(-15.9, -110) * mm});
            skLineSegment(sketch, "E91.MirrorCS", {"start": v(-15.9, -98) * mm, "end": v(-15.9, -110) * mm});
            skLineSegment(sketch, "E92.MirrorCS", {"start": v(-33.9, -80) * mm, "end": v(-15.9, -98) * mm});
            skCircle(sketch, "E93.MirrorC", {"center": v(-3.69, -118.7) * mm, "radius": 6 * mm});
            skLineSegment(sketch, "E94.MirrorCS", {"start": v(-3.69, -118.7) * mm, "end": v(-3.69, -80) * mm, "construction": true});
            skSolve(sketch);
        }
        {
            var Q0;
            Q0 = qSketchRegion(id + "F16", true);
            extrude(context, id + "F17", {"entities" : qUnion([Q0]), "depth" : 25 * mm});
        }
        {
            var Q0;
            Q0 = qSketchRegion(id + "F16", true);
            extrude(context, id + "F18", {"entities" : qUnion([Q0]), "depth" : 25 * mm});
        }
        {
            var Q0;
            Q0 = qSketchRegion(id + "F16", true);
            extrude(context, id + "F19", {"entities" : qUnion([Q0]), "depth" : 25 * mm});
        }
    });
